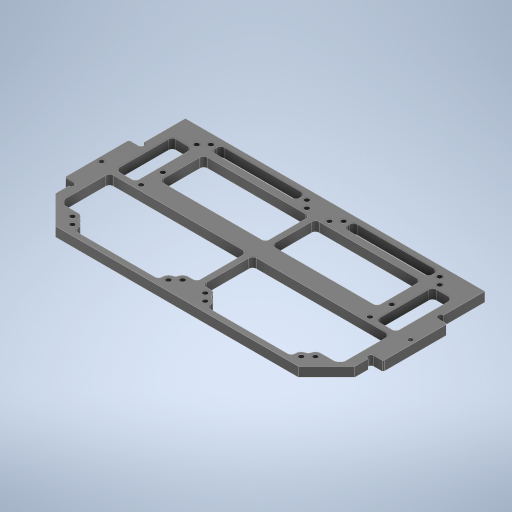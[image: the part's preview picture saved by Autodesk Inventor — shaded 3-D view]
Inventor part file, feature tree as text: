
AUTODESK INVENTOR PART (.ipt)
format: ipt  version: 2024.2 (Build 282272000, 272)  size: 577,536 bytes
history: native  units: mm
features: sketch x1, extrude x1, chamfer x1, hole x1, plane x1
ambient origin geometry x8: Origin, YZ Plane, XZ Plane, XY Plane, X Axis, Y Axis, Z Axis, Center Point
bodies: Solid1 (feature_tree)
feature tree (5):
  sketch  "Sketch1"  dims[d1=159.0mm d2=1.5mm d3=5.0mm d12=5.0mm d13=0.0mm d36=25.0mm d42=58.5mm d43=66.0mm d44=82.0mm d45=67.0mm d49=2.459mm d50=6.0mm d51=6.5mm d52=2.5mm d53=90.0deg d54=8.0mm d55=20.594885mm d58=0.5mm d59=2.0mm d60=45.0deg d67=5.0mm d70=42.0mm d71=84.0mm d73=25.0mm d75=12.0mm d88=2.5mm d89=6.0mm d90=4.0mm d91=2.0mm d92=90.0deg d93=8.0mm d94=20.594885mm d102=6.0mm d108=3.0mm d116=3.0mm d118=6.0mm d122=2.0mm d131=1.5mm d147=15.0mm d148=45.0deg d150=3.0mm d151=51.0mm d153=36.5mm d156=25.5mm d159=11.5mm d160=19.5mm d161=31.0mm d162=107.0mm d163=3.0mm]
  extrude  "Extrusion1"  Depth=1.5mm
  chamfer  "C0.5"  Distance=5.0mm
  hole  "Phi2.5"  [1 undecoded]
  plane  "Work Plane1"
note: 1 required parameter value undecoded (feature->parameter linkage not recoverable at this tier; creation-order binding heuristic only, values carry confidence <= 0.55)
